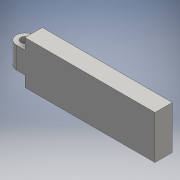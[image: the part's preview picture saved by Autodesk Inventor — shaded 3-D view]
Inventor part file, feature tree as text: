
AUTODESK INVENTOR PART (.ipt)
format: ipt  version: 2016 (Build 200138000, 138)  size: 109,056 bytes
history: native  units: mm
features: extrude x2, fillet x2, other x1, sketch x1
ambient origin geometry x8: Origin, YZ Plane, XZ Plane, XY Plane, X Axis, Y Axis, Z Axis, Center Point
bodies: Body1 (feature_tree)
feature tree (6):
  other  "ソリッド1"
  extrude  "押し出し1"  Depth=30.0mm
  extrude  "押し出し2"  Depth=10.0mm
  fillet  "フィレット1"  Radius=4.0mm
  fillet  "フィレット2"  Radius=5.0mm
  sketch  "スケッチ2"
